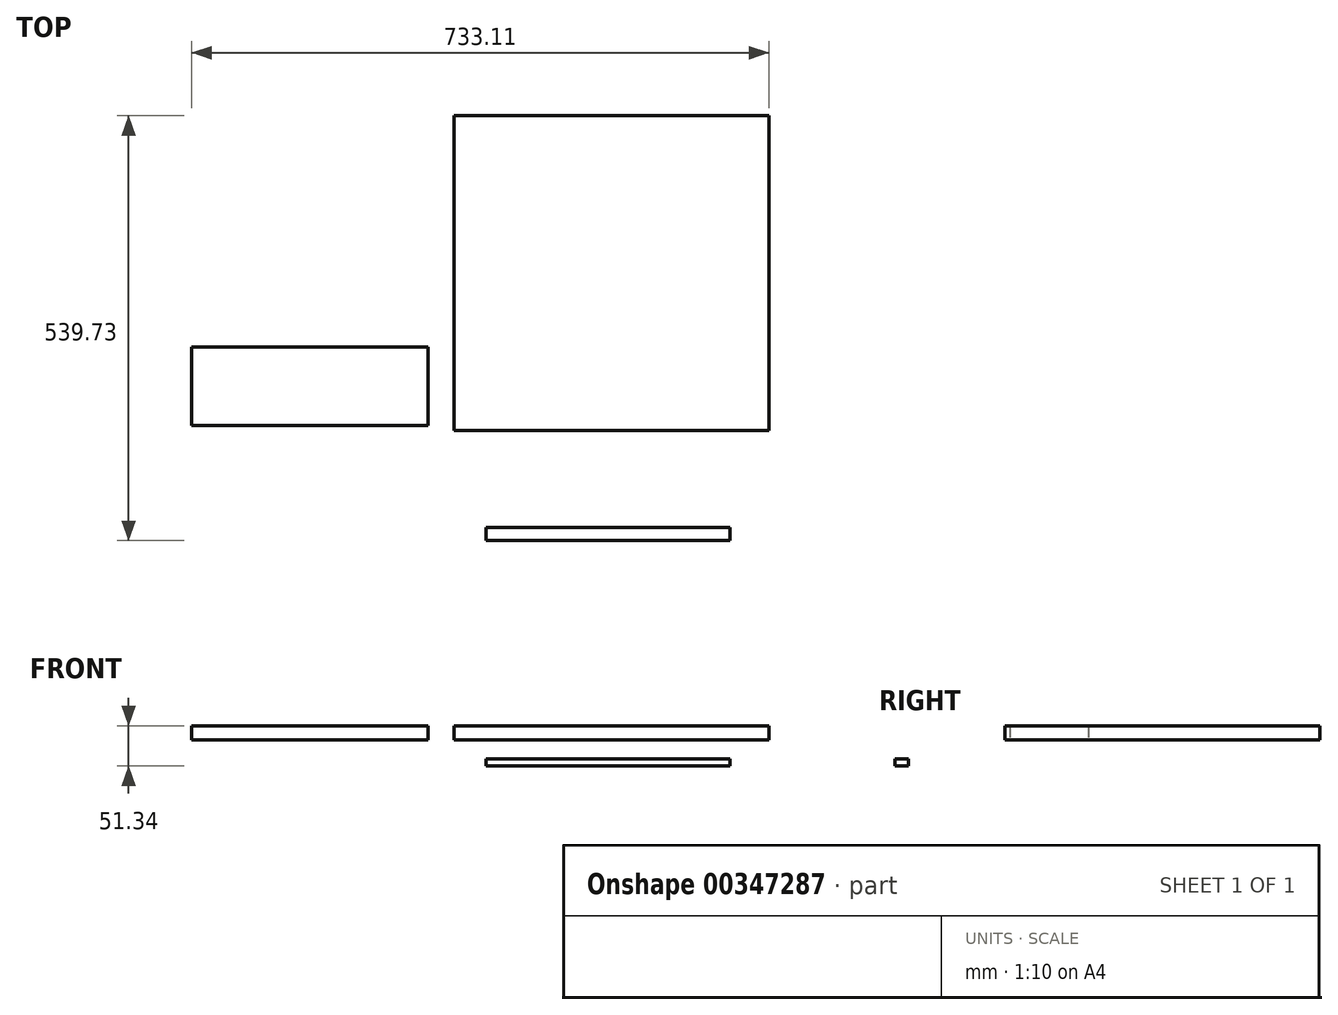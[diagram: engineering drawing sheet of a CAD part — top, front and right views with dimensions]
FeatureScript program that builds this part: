
annotation { "Feature Type Name" : "Feature", "Feature Type Description" : "" }
export const myFeature = defineFeature(function(context is Context, id is Id, definition is map)
    precondition{}
    {
        {
            var Q0;
            Q0=qCreatedBy(makeId("Top.planeOp"),FACE);
            var sketch = newSketch(context, id + "F0", { "sketchPlane" : qUnion([Q0])});
            skLineSegment(sketch, "E0.bottom", {"start": v(-40.5, -27.06) * mm, "end": v(359.5, -27.06) * mm});
            skLineSegment(sketch, "E0.top", {"start": v(-40.5, 372.94) * mm, "end": v(359.5, 372.94) * mm});
            skLineSegment(sketch, "E0.left", {"start": v(-40.5, -27.06) * mm, "end": v(-40.5, 372.94) * mm});
            skLineSegment(sketch, "E0.right", {"start": v(359.5, -27.06) * mm, "end": v(359.5, 372.94) * mm});
            skSolve(sketch);
        }
        {
            var Q0;
            Q0=makeQuery(id+"F0.imprint","IMPRINT",FACE,{"disambiguationData":[TD([[makeQuery(id+"F0.imprint","IMPRINT",EDGE,{"derivedFrom":sQuery(id+"F0.wireOp",EDGE,"E0.bottom")}),1.0]])]});
            extrude(context, id + "F1", {"entities" : qUnion([Q0]), "depth" : 18 * mm});
        }
        {
            var Q0;
            Q0=qCreatedBy(makeId("Right.planeOp"),FACE);
            var sketch = newSketch(context, id + "F2", { "sketchPlane" : qUnion([Q0])});
            skLineSegment(sketch, "E1.bottom", {"start": v(-166.79, -33.34) * mm, "end": v(-149.79, -33.34) * mm});
            skLineSegment(sketch, "E1.top", {"start": v(-166.79, -23.94) * mm, "end": v(-149.79, -23.94) * mm});
            skLineSegment(sketch, "E1.left", {"start": v(-166.79, -33.34) * mm, "end": v(-166.79, -23.94) * mm});
            skLineSegment(sketch, "E1.right", {"start": v(-149.79, -33.34) * mm, "end": v(-149.79, -23.94) * mm});
            skSolve(sketch);
        }
        {
            var Q0;
            Q0 = qSketchRegion(id + "F2", true);
            extrude(context, id + "F3", {"entities" : qUnion([Q0]), "depth" : 310 * mm});
        }
        {
            var Q0;
            Q0=qCreatedBy(makeId("Top.planeOp"),FACE);
            var sketch = newSketch(context, id + "F4", { "sketchPlane" : qUnion([Q0])});
            skLineSegment(sketch, "E2.bottom", {"start": v(-73.6, -20.57) * mm, "end": v(-373.6, -20.57) * mm});
            skLineSegment(sketch, "E2.top", {"start": v(-73.6, 79.43) * mm, "end": v(-373.6, 79.43) * mm});
            skLineSegment(sketch, "E2.left", {"start": v(-73.6, -20.57) * mm, "end": v(-73.6, 79.43) * mm});
            skLineSegment(sketch, "E2.right", {"start": v(-373.6, -20.57) * mm, "end": v(-373.6, 79.43) * mm});
            skSolve(sketch);
        }
        {
            var Q0;
            Q0=makeQuery(id+"F4.imprint","IMPRINT",FACE,{"disambiguationData":[TD([[makeQuery(id+"F4.imprint","IMPRINT",EDGE,{"derivedFrom":sQuery(id+"F4.wireOp",EDGE,"E2.bottom")}),-1.0]])]});
            extrude(context, id + "F5", {"entities" : qUnion([Q0]), "depth" : 18 * mm});
        }
    });
